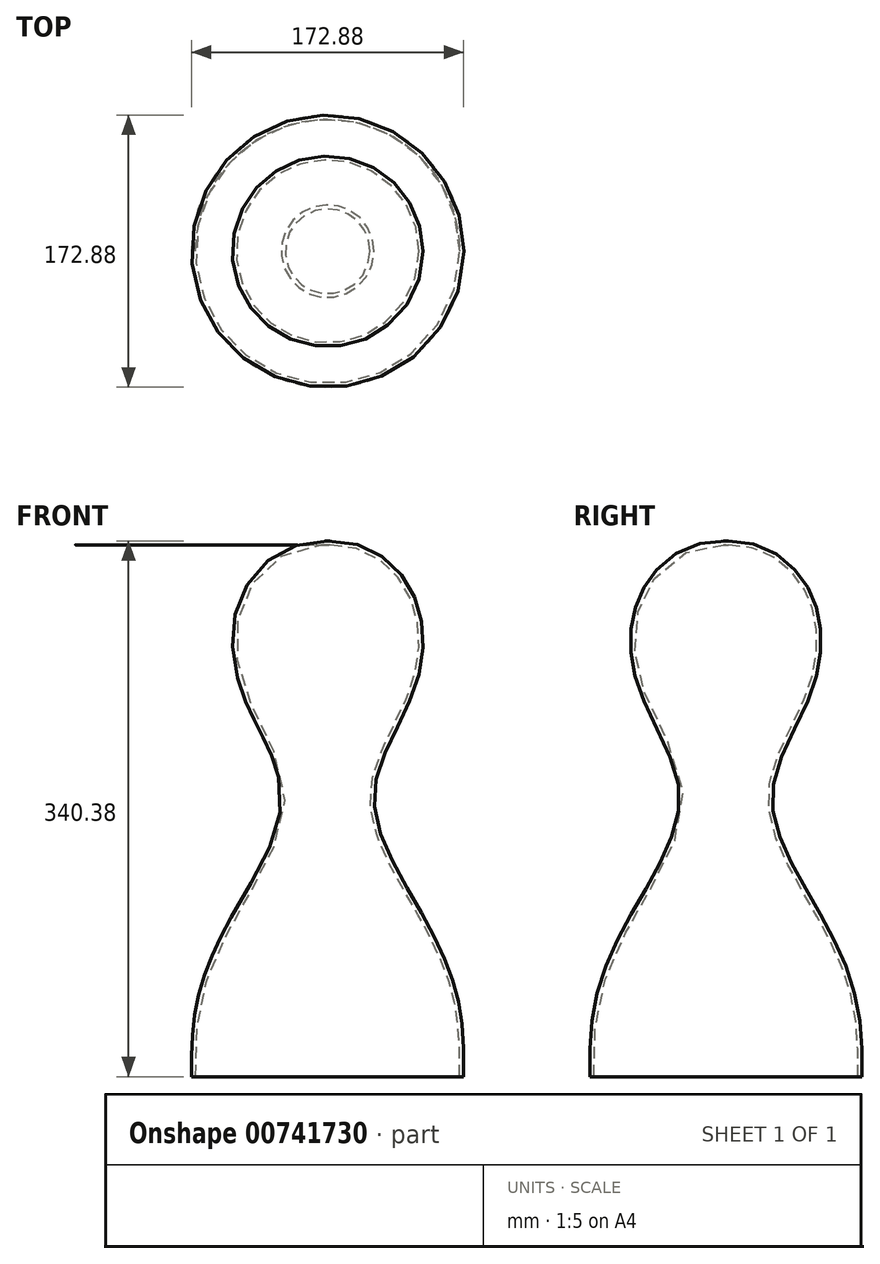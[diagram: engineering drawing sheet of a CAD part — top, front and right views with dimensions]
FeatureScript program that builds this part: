
annotation { "Feature Type Name" : "Feature", "Feature Type Description" : "" }
export const myFeature = defineFeature(function(context is Context, id is Id, definition is map)
    precondition{}
    {
        {
            var Q0;
            Q0=qCreatedBy(makeId("Front.planeOp"),FACE);
            var sketch = newSketch(context, id + "F0", { "sketchPlane" : qUnion([Q0])});
            skLineSegment(sketch, "E0", {"start": v(0, 0) * mm, "end": v(86.36, 0) * mm});
            skLineSegment(sketch, "E1", {"start": v(0, 0) * mm, "end": v(0, 340.36) * mm});
            skFitSpline(sketch, "E2", {"points": [v(86.36, 0) * mm, v(81.1, 55.66) * mm, v(58.36, 106.23) * mm, v(29.46, 177.8) * mm, v(55.06, 246.08) * mm, v(53.7, 307.68) * mm, v(0, 340.36) * mm], "startDerivative": vector(8.55, 448.7) * mm, "endDerivative": vector(-475.68, -11.47) * mm});
            skFitSpline(sketch, "E3.MirrorCS", {"points": [v(-86.36, 0) * mm, v(-81.1, 55.66) * mm, v(-58.36, 106.23) * mm, v(-29.46, 177.8) * mm, v(-55.06, 246.08) * mm, v(-53.7, 307.68) * mm, v(0, 340.36) * mm], "startDerivative": vector(-8.55, 448.7) * mm, "endDerivative": vector(475.68, -11.47) * mm});
            skLineSegment(sketch, "E4", {"start": v(29.46, 177.8) * mm, "end": v(0, 177.8) * mm, "construction": true});
            skPoint(sketch, "E5", {"position": v(41.44, 216.35) * mm});
            skSolve(sketch);
        }
        {
            var Q0;
            Q0=makeQuery(id+"F0.imprint","IMPRINT",FACE,{"disambiguationData":[TD([[makeQuery(id+"F0.imprint","IMPRINT",EDGE,{"derivedFrom":sQuery(id+"F0.wireOp",EDGE,"E0")}),1.0]])]});
            var Q1;
            Q1=sQuery(id+"F0.wireOp",EDGE,"E2");
            var Q2;
            Q2=sQuery(id+"F0.wireOp",EDGE,"E0");
            var Q3;
            Q3=sQuery(id+"F0.wireOp",EDGE,"E1");
            revolve(context, id + "F1", {"surfaceOperationType" : NewSurfaceOperationType.NEW, "entities" : qUnion([Q0]), "surfaceEntities" : qUnion([Q1, Q2]), "axis" : qUnion([Q3]), "revolveType" : RevolveType.FULL});
        }
        {
            var Q0;
            Q0=makeQuery(id+"F1.opRevolve","SWEPT_FACE",FACE,{"disambiguationData":[OSD([sQuery(id+"F0.wireOp",EDGE,"E0")])]});
            shell(context, id + "F2", {"entities" : qUnion([Q0]), "thickness" : 2.54 * mm});
        }
    });
